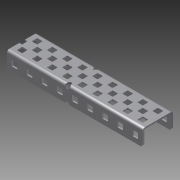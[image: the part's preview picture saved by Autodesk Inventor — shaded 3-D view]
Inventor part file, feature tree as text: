
AUTODESK INVENTOR PART (.ipt)
format: ipt  version: 2014 SP1 (Build 180222100, 222)  size: 740,352 bytes
history: native  units: in
note: dims shown in document units (in); Inventor stores cm internally (conversion verified against a paired STEP export)
features: other x1, imported_body x1, extrude x1, sketch x1
ambient origin geometry x8: Origin, YZ Plane, XZ Plane, XY Plane, X Axis, Y Axis, Z Axis, Center Point
bodies: Body1 (feature_tree)
feature tree (4):
  parser-record x1  (decoder bookkeeping rows leaked as tree rows — omitted from the tree; the rows remain in map.json)
  imported_body  "Base1"
  extrude  "Extrusion1"  Depth=0.5in TaperAngle=0.0deg
  sketch  "Sketch2"  dims[d0=0.5in d1=1.0in d2=0.0in]
